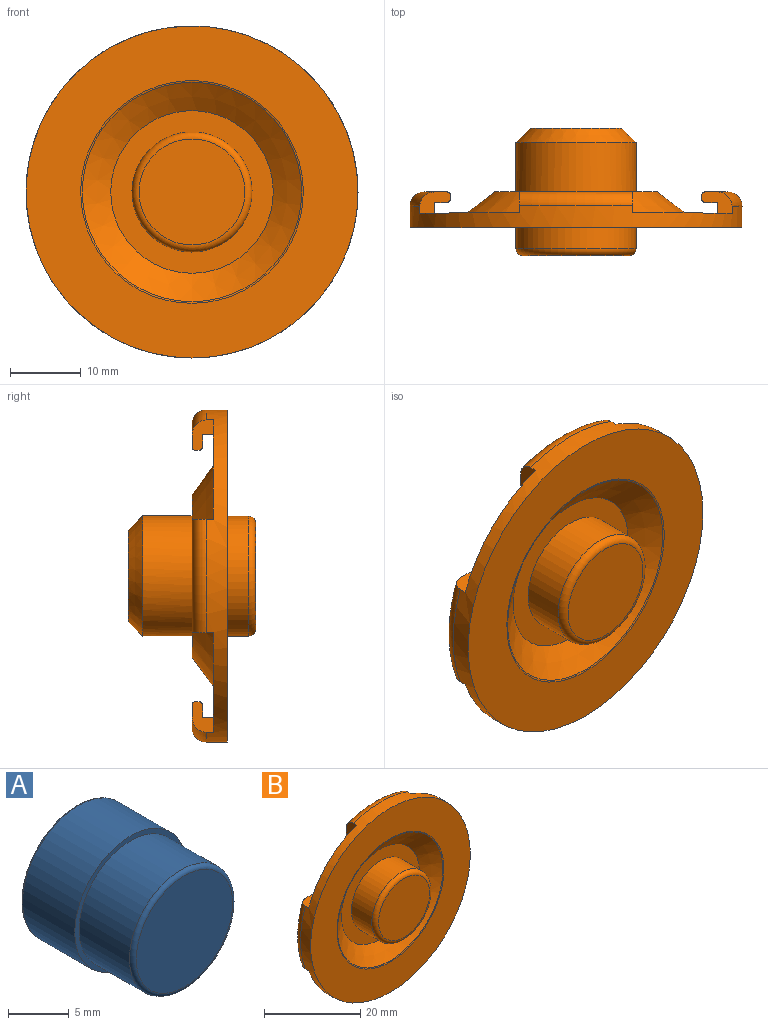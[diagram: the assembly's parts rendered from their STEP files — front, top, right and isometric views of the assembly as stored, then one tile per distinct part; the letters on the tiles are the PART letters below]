
ASSEMBLY  parts=2 mates=1
PART A: 9 faces, bbox 14.1x12.5x14.1 mm
  f0: cylinder r=6mm len=12mm, axis (0,-1,0), area 220.5mm2, adj f1,f6
  f1: plane 13x13mm, normal (0,-1,0), area 19.6mm2, adj f0,f2
  f2: cylinder r=6.5mm len=13mm, axis (0,-1,0), area 248.7mm2, adj f1,f3
  f3: torus R=6.34mm, axis (0,-1,0), area 10.2mm2, adj f2,f4
  f4: plane 12.68x12.68mm, normal (0,1,0), area 114.3mm2, adj f3,f7
  f5: plane 11.2x11.2mm, normal (0,-1,0), area 98.5mm2, adj f6
  f6: torus R=5.6mm, axis (0,-1,0), area 23.1mm2, adj f0,f5
  f7: cylinder r=1.95mm len=5mm, axis (0,1,0), area 61.3mm2, adj f4,f8
  f8: plane 3.9x3.9mm, normal (0,1,0), area 11.9mm2, adj f7
PART B: 64 faces, bbox 50.9x18x50.9 mm
  f0: cylinder r=19.5mm len=16mm, axis (0,-1,0), area 8.2mm2, adj f8,f9,f42,f44
  f1: cylinder r=19.5mm len=16mm, axis (0,-1,0), area 8.2mm2, adj f10,f11,f41,f43
  f2: cylinder r=19.5mm len=16mm, axis (0,-1,0), area 8.2mm2, adj f4,f5,f40,f46
  f3: cylinder r=19.5mm len=16mm, axis (0,-1,0), area 8.2mm2, adj f6,f7,f39,f45
  f4: plane 4.31x3mm, normal (0,0,1), area 8.4mm2, adj f2,f12,f13,f23,f36,f37,f38,f40
  f5: plane 4.31x3mm, normal (0,0,-1), area 8.4mm2, adj f2,f12,f13,f23,f36,f37,f38,f40
  f6: plane 4.31x3mm, normal (-1,0,0), area 8.4mm2, adj f3,f12,f13,f24,f33,f34,f35,f39
  f7: plane 4.31x3mm, normal (1,0,0), area 8.4mm2, adj f3,f12,f13,f24,f33,f34,f35,f39
  f8: plane 4.31x3mm, normal (0,0,-1), area 8.4mm2, adj f0,f12,f13,f25,f30,f31,f32,f42
  f9: plane 4.31x3mm, normal (0,0,1), area 8.4mm2, adj f0,f12,f13,f25,f30,f31,f32,f42
  f10: plane 4.31x3mm, normal (1,0,0), area 8.4mm2, adj f1,f12,f13,f26,f27,f28,f29,f41
  f11: plane 4.31x3mm, normal (-1,0,0), area 8.4mm2, adj f1,f12,f13,f26,f27,f28,f29,f41
  f12: plane 44.19x44.19mm, normal (0,1,0), area 418mm2, adj f4,f5,f6,f7,f8,f9,f10,f11
  f13: cylinder r=23.5mm len=47mm, axis (0,1,0), area 360.6mm2, adj f4,f5,f6,f7,f8,f9,f10,f11
  f14: cone r=11.5mm half-angle=54deg, axis (0,-1,0), area 421.9mm2, adj f47,f60
  f15: plane 47x47mm, normal (0,-1,0), area 955.1mm2, adj f13,f47
  f16: cylinder r=19.5mm len=39mm, axis (0,-1,0), area 122.5mm2, adj f12,f21
  f17: plane 13x13mm, normal (0,1,0), area 64.8mm2, adj f22,f52
  f18: cylinder r=8.5mm len=17mm, axis (0,1,0), area 373.8mm2, adj f19,f22
  f19: plane 23x23mm, normal (0,1,0), area 188.5mm2, adj f18,f20
  f20: cone r=11.5mm half-angle=54deg, axis (0,-1,0), area 608.9mm2, adj f19,f21
  f21: plane 39x39mm, normal (0,1,0), area 286.7mm2, adj f16,f20
  f22: cone r=6.5mm half-angle=45deg, axis (0,-1,0), area 133.3mm2, adj f17,f18
  f23: plane 16x3.17mm, normal (0,1,0), area 24.6mm2, adj f4,f5,f46,f51
  f24: plane 16x3.17mm, normal (0,1,0), area 24.6mm2, adj f6,f7,f45,f50
  f25: plane 16x3.17mm, normal (0,1,0), area 24.6mm2, adj f8,f9,f44,f49
  f26: plane 16x3.17mm, normal (0,1,0), area 24.6mm2, adj f10,f11,f43,f48
  f27: revolved ~16.15x1.75mm, area 5.3mm2, adj f10,f11,f28,f29
  f28: cylinder r=21.63mm len=16mm, axis (0,-1,0), area 20.9mm2, adj f10,f11,f12,f27
  f29: plane 16x3.1mm, normal (0,-1,0), area 23.4mm2, adj f10,f11,f27,f41
  f30: revolved ~16.15x1.75mm, area 5.3mm2, adj f8,f9,f31,f32
  f31: cylinder r=21.63mm len=16mm, axis (0,-1,0), area 20.9mm2, adj f8,f9,f12,f30
  f32: plane 16x3.1mm, normal (0,-1,0), area 23.4mm2, adj f8,f9,f30,f42
  f33: revolved ~16.15x1.75mm, area 5.3mm2, adj f6,f7,f34,f35
  f34: cylinder r=21.63mm len=16mm, axis (0,-1,0), area 20.9mm2, adj f6,f7,f12,f33
  f35: plane 16x3.1mm, normal (0,-1,0), area 23.4mm2, adj f6,f7,f33,f39
  f36: plane 16x3.1mm, normal (0,-1,0), area 23.4mm2, adj f4,f5,f38,f40
  f37: cylinder r=21.63mm len=16mm, axis (0,-1,0), area 20.9mm2, adj f4,f5,f12,f38
  f38: revolved ~16.15x1.75mm, area 5.3mm2, adj f4,f5,f36,f37
  f39: torus R=20mm, axis (0,-1,0), area 12.9mm2, adj f3,f6,f7,f35
  f40: torus R=20mm, axis (0,-1,0), area 12.9mm2, adj f2,f4,f5,f36
  f41: torus R=20mm, axis (0,-1,0), area 12.9mm2, adj f1,f10,f11,f29
  f42: torus R=20mm, axis (0,-1,0), area 12.9mm2, adj f0,f8,f9,f32
  f43: torus R=20mm, axis (0,1,0), area 12.9mm2, adj f1,f10,f11,f26
  f44: torus R=20mm, axis (0,1,0), area 12.9mm2, adj f0,f8,f9,f25
  f45: torus R=20mm, axis (0,1,0), area 12.9mm2, adj f3,f6,f7,f24
  f46: torus R=20mm, axis (0,1,0), area 12.9mm2, adj f2,f4,f5,f23
  f47: torus R=15.76mm, axis (0,-1,0), area 24.7mm2, adj f14,f15
  f48: torus R=21.5mm, axis (0,1,0), area 51.4mm2, adj f10,f11,f13,f26
  f49: torus R=21.5mm, axis (0,1,0), area 51.4mm2, adj f8,f9,f13,f25
  f50: torus R=21.5mm, axis (0,1,0), area 51.4mm2, adj f6,f7,f13,f24
  f51: torus R=21.5mm, axis (0,1,0), area 51.4mm2, adj f4,f5,f13,f23
  f52: cone r=4.65mm half-angle=10deg, axis (0,-1,0), area 110.7mm2, adj f17,f57
  f53: cylinder r=6mm len=12mm, axis (0,-1,0), area 220.5mm2, adj f54,f59
  f54: plane 13x13mm, normal (0,1,0), area 19.6mm2, adj f53,f55
  f55: cylinder r=6.5mm len=13mm, axis (0,-1,0), area 248.7mm2, adj f54,f56
  f56: torus R=6.34mm, axis (0,-1,0), area 10.2mm2, adj f55,f57
  f57: plane 12.68x12.68mm, normal (0,-1,0), area 39.1mm2, adj f52,f56
  f58: plane 11.2x11.2mm, normal (0,1,0), area 98.5mm2, adj f59
  f59: torus R=5.6mm, axis (0,-1,0), area 23.1mm2, adj f53,f58
  f60: plane 23x23mm, normal (0,-1,0), area 188.5mm2, adj f14,f63
  f61: plane 15x15mm, normal (0,-1,0), area 176.7mm2, adj f62
  f62: torus R=7.5mm, axis (0,-1,0), area 80.3mm2, adj f61,f63
  f63: cylinder r=8.5mm len=17mm, axis (0,-1,0), area 320.4mm2, adj f60,f62
PLACE A t=(22.22,7.03,37.41)mm
PLACE B t=(22.22,7.03,37.41)mm fixed
MATE fastened B.f53 <-> A.f0  axis (0,1,0) through (22.22,-8.97,37.41)mm
